# Revit family: SoapDispenser_Metlam_BenchMounted
name_source: partatom
category: Generic Models
revit_build: Autodesk Revit Architecture 2013 (Build: 20120221_2030(x64)
units: mm (PartAtom-declared; Revit-internal decimal feet)

## types (2) — shared parameters
Assembly Code = E1090900
Default Elevation = 900 mm  [stored 2.95276 ft]
Depth = 82 mm  [stored 0.269029 ft]
Description = Lav-Basin Soap Dispenser
FilterObject_ANZRS = Soap Dispenser
Height = 426 mm  [stored 1.39764 ft]
Keywords = CAPACITY 950ml
Manufacturer = Metlam
Material Container = Plastic, Opaque White
Material Mechanism = Plastic, Black
Material Nozzle = Plastic, Chrome Plated
ModifiedIssue_ANZRS = 130318.01 $
Product Code = ML 628-4
StyleOrType_ANZRS = Sanitary Ware
URL = http://www.metlam.com.au
Width = 82 mm  [stored 0.269029 ft]

## per-type parameters (varying)
| type | 100mm Spout | 150mm Spout | Model |
| Metlam Bench Mounted 100 | Yes | No | Bench Mounted 100 |
| Metlam Bench Mounted 150 | No | Yes | Bench Mounted 150 |

note: [stored X ft] marks values corroborated as IEEE doubles in the binary element streams (Revit-internal decimal feet)

## geometry (parser evidence)
native form markers: Blend x12, Sweep x1
no freeform markers — native parametric forms only
